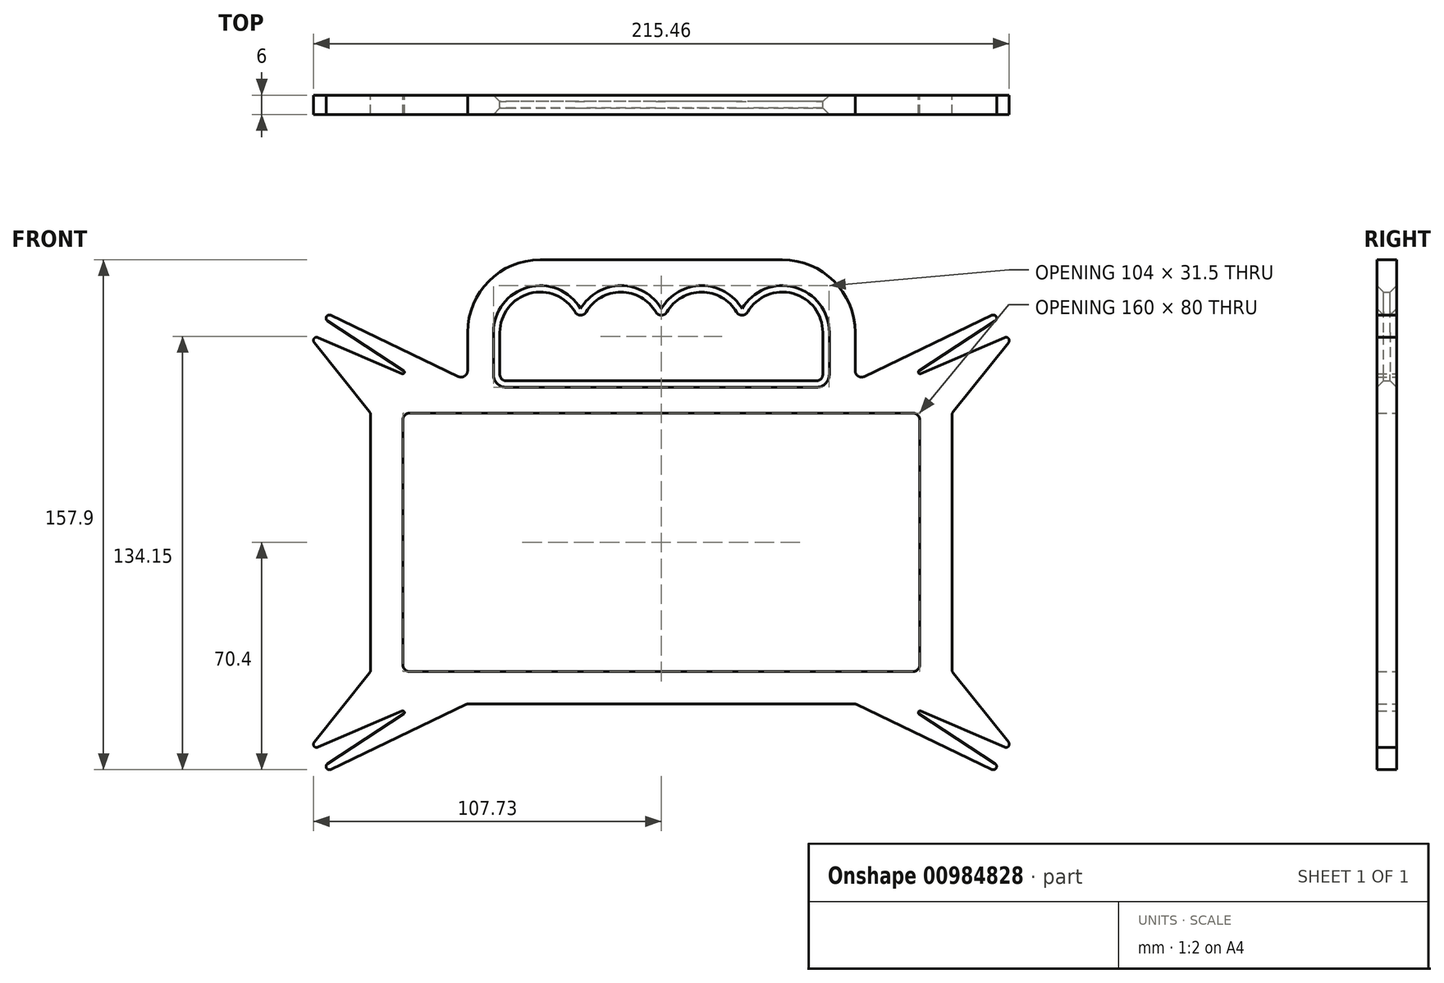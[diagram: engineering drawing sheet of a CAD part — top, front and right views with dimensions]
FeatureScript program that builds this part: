
annotation { "Feature Type Name" : "Feature", "Feature Type Description" : "" }
export const myFeature = defineFeature(function(context is Context, id is Id, definition is map)
    precondition{}
    {
        {
            var Q0;
            Q0=qCreatedBy(makeId("Front.planeOp"),FACE);
            var sketch = newSketch(context, id + "F0", { "sketchPlane" : qUnion([Q0])});
            skLineSegment(sketch, "E0.bottom", {"start": v(78, 40) * mm, "end": v(-78, 40) * mm});
            skLineSegment(sketch, "E0.top", {"start": v(78, -40) * mm, "end": v(-78, -40) * mm});
            skLineSegment(sketch, "E0.left", {"start": v(80, 38) * mm, "end": v(80, -38) * mm});
            skLineSegment(sketch, "E0.right", {"start": v(-80, 38) * mm, "end": v(-80, -38) * mm});
            skPoint(sketch, "E0.middle", {"position": v(0, 0) * mm});
            skLineSegment(sketch, "E1.top", {"start": v(60, -50) * mm, "end": v(-60, -50) * mm});
            skLineSegment(sketch, "E1.left", {"start": v(90, 39.3) * mm, "end": v(90, -40) * mm});
            skLineSegment(sketch, "E1.right", {"start": v(-90, 40) * mm, "end": v(-90, -40) * mm});
            skLineSegment(sketch, "E2", {"start": v(80.25, 52.25) * mm, "end": v(106.33, 63.43) * mm});
            skLineSegment(sketch, "E3", {"start": v(107.5, 61.88) * mm, "end": v(90.44, 40.55) * mm});
            skPoint(sketch, "E4.visualSharp", {"position": v(110, 65) * mm});
            skArc(sketch, "E4.filletArc", {"start": v(107.5, 61.88) * mm, "mid": v(107.52, 63.11) * mm, "end": v(106.33, 63.43) * mm});
            skLineSegment(sketch, "E5", {"start": v(79.78, 53.13) * mm, "end": v(103.37, 68.56) * mm});
            skLineSegment(sketch, "E6", {"start": v(102.39, 70.3) * mm, "end": v(62.86, 51.37) * mm});
            skPoint(sketch, "E7.visualSharp", {"position": v(75, 50) * mm});
            skArc(sketch, "E7.filletArc", {"start": v(79.78, 53.13) * mm, "mid": v(79.62, 52.47) * mm, "end": v(80.25, 52.25) * mm});
            skPoint(sketch, "E8.visualSharp", {"position": v(115.95, 76.8) * mm});
            skArc(sketch, "E8.filletArc", {"start": v(103.37, 68.56) * mm, "mid": v(103.7, 69.9) * mm, "end": v(102.39, 70.3) * mm});
            skPoint(sketch, "E9.newPointA", {"position": v(60, 50) * mm});
            skPoint(sketch, "E9.newPointB", {"position": v(90, 50) * mm});
            skPoint(sketch, "E10.visualSharp", {"position": v(80, 40) * mm});
            skArc(sketch, "E10.filletArc", {"start": v(80, 38) * mm, "mid": v(79.41, 39.41) * mm, "end": v(78, 40) * mm});
            skPoint(sketch, "E11.newPointA", {"position": v(90, 40) * mm});
            skArc(sketch, "E11.filletArc", {"start": v(90.44, 40.55) * mm, "mid": v(90.11, 39.96) * mm, "end": v(90, 39.3) * mm});
            skArc(sketch, "E12.MirrorCS", {"start": v(-79.78, 53.13) * mm, "mid": v(-79.62, 52.47) * mm, "end": v(-80.25, 52.25) * mm});
            skArc(sketch, "E13.MirrorCS", {"start": v(-107.5, 61.88) * mm, "mid": v(-107.52, 63.11) * mm, "end": v(-106.33, 63.43) * mm});
            skArc(sketch, "E14.MirrorCS", {"start": v(-80, 38) * mm, "mid": v(-79.41, 39.41) * mm, "end": v(-78, 40) * mm});
            skArc(sketch, "E15.MirrorCS", {"start": v(-103.37, 68.56) * mm, "mid": v(-103.7, 69.9) * mm, "end": v(-102.39, 70.3) * mm});
            skArc(sketch, "E16.MirrorCS", {"start": v(-59.55, 50) * mm, "mid": v(-59.99, 50.05) * mm, "end": v(-60.4, 50.2) * mm});
            skArc(sketch, "E17.MirrorCS", {"start": v(-90.44, 40.55) * mm, "mid": v(-90.11, 39.96) * mm, "end": v(-90, 39.3) * mm});
            skPoint(sketch, "E18.MirrorP", {"position": v(-110, 65) * mm});
            skLineSegment(sketch, "E19.MirrorCS", {"start": v(-80.25, 52.25) * mm, "end": v(-106.33, 63.43) * mm});
            skPoint(sketch, "E20.MirrorP", {"position": v(-80, 40) * mm});
            skPoint(sketch, "E21.MirrorP", {"position": v(-90, 40) * mm});
            skPoint(sketch, "E22.MirrorP", {"position": v(-75, 50) * mm});
            skPoint(sketch, "E23.MirrorP", {"position": v(-60, 50) * mm});
            skLineSegment(sketch, "E24.MirrorCS", {"start": v(-102.39, 70.3) * mm, "end": v(-62.86, 51.37) * mm});
            skLineSegment(sketch, "E25.MirrorCS", {"start": v(-107.5, 61.88) * mm, "end": v(-90.44, 40.55) * mm});
            skLineSegment(sketch, "E26.MirrorCS", {"start": v(-79.78, 53.13) * mm, "end": v(-103.37, 68.56) * mm});
            skPoint(sketch, "E27.MirrorP", {"position": v(-115.95, 76.8) * mm});
            skPoint(sketch, "E28.MirrorP", {"position": v(-90, 50) * mm});
            skLineSegment(sketch, "E29.MirrorCS", {"start": v(-90, 39.3) * mm, "end": v(-90, -40) * mm});
            skArc(sketch, "E30.MirrorCS", {"start": v(-90.44, -40.55) * mm, "mid": v(-90.11, -39.96) * mm, "end": v(-90, -39.3) * mm});
            skArc(sketch, "E31.MirrorCS", {"start": v(-59.55, -50) * mm, "mid": v(-59.99, -50.05) * mm, "end": v(-60.4, -50.2) * mm});
            skArc(sketch, "E32.MirrorCS", {"start": v(-107.5, -61.88) * mm, "mid": v(-107.52, -63.11) * mm, "end": v(-106.33, -63.43) * mm});
            skArc(sketch, "E33.MirrorCS", {"start": v(-103.37, -68.56) * mm, "mid": v(-103.7, -69.9) * mm, "end": v(-102.39, -70.3) * mm});
            skArc(sketch, "E34.MirrorCS", {"start": v(-79.78, -53.13) * mm, "mid": v(-79.62, -52.47) * mm, "end": v(-80.25, -52.25) * mm});
            skArc(sketch, "E35.MirrorCS", {"start": v(-80, -38) * mm, "mid": v(-79.41, -39.41) * mm, "end": v(-78, -40) * mm});
            skArc(sketch, "E36.MirrorCS", {"start": v(79.78, -53.13) * mm, "mid": v(79.62, -52.47) * mm, "end": v(80.25, -52.25) * mm});
            skArc(sketch, "E37.MirrorCS", {"start": v(107.5, -61.88) * mm, "mid": v(107.52, -63.11) * mm, "end": v(106.33, -63.43) * mm});
            skArc(sketch, "E38.MirrorCS", {"start": v(103.37, -68.56) * mm, "mid": v(103.7, -69.9) * mm, "end": v(102.39, -70.3) * mm});
            skArc(sketch, "E39.MirrorCS", {"start": v(59.55, -50) * mm, "mid": v(59.99, -50.05) * mm, "end": v(60.4, -50.2) * mm});
            skArc(sketch, "E40.MirrorCS", {"start": v(80, -38) * mm, "mid": v(79.41, -39.41) * mm, "end": v(78, -40) * mm});
            skArc(sketch, "E41.MirrorCS", {"start": v(90.44, -40.55) * mm, "mid": v(90.11, -39.96) * mm, "end": v(90, -39.3) * mm});
            skPoint(sketch, "E42.MirrorP", {"position": v(-90, -40) * mm});
            skPoint(sketch, "E43.MirrorP", {"position": v(-110, -65) * mm});
            skPoint(sketch, "E44.MirrorP", {"position": v(-60, -50) * mm});
            skPoint(sketch, "E45.MirrorP", {"position": v(-80, -40) * mm});
            skLineSegment(sketch, "E46.MirrorCS", {"start": v(-80.25, -52.25) * mm, "end": v(-106.33, -63.43) * mm});
            skLineSegment(sketch, "E47.MirrorCS", {"start": v(-107.5, -61.88) * mm, "end": v(-90.44, -40.55) * mm});
            skLineSegment(sketch, "E48.MirrorCS", {"start": v(-79.78, -53.13) * mm, "end": v(-103.37, -68.56) * mm});
            skPoint(sketch, "E49.MirrorP", {"position": v(-75, -50) * mm});
            skLineSegment(sketch, "E50.MirrorCS", {"start": v(-102.39, -70.3) * mm, "end": v(-60.4, -50.2) * mm});
            skPoint(sketch, "E51.MirrorP", {"position": v(-115.95, -76.8) * mm});
            skPoint(sketch, "E52.MirrorP", {"position": v(-90, -50) * mm});
            skLineSegment(sketch, "E53.MirrorCS", {"start": v(102.39, -70.3) * mm, "end": v(60.4, -50.2) * mm});
            skLineSegment(sketch, "E54.MirrorCS", {"start": v(79.78, -53.13) * mm, "end": v(103.37, -68.56) * mm});
            skPoint(sketch, "E55.MirrorP", {"position": v(115.95, -76.8) * mm});
            skLineSegment(sketch, "E56.MirrorCS", {"start": v(107.5, -61.88) * mm, "end": v(90.44, -40.55) * mm});
            skPoint(sketch, "E57.MirrorP", {"position": v(60, -50) * mm});
            skLineSegment(sketch, "E58.MirrorCS", {"start": v(80.25, -52.25) * mm, "end": v(106.33, -63.43) * mm});
            skLineSegment(sketch, "E59.MirrorCS", {"start": v(59.55, -50) * mm, "end": v(-60, -50) * mm});
            skPoint(sketch, "E60.MirrorP", {"position": v(110, -65) * mm});
            skLineSegment(sketch, "E61.MirrorCS", {"start": v(-59.55, -50) * mm, "end": v(60, -50) * mm});
            skPoint(sketch, "E62.MirrorP", {"position": v(75, -50) * mm});
            skPoint(sketch, "E63.MirrorP", {"position": v(80, -40) * mm});
            skPoint(sketch, "E64.MirrorP", {"position": v(90, -50) * mm});
            skPoint(sketch, "E65.MirrorP", {"position": v(90, -40) * mm});
            skLineSegment(sketch, "E66.MirrorCS", {"start": v(-78, -40) * mm, "end": v(78, -40) * mm});
            skLineSegment(sketch, "E67.bottom", {"start": v(40, 50) * mm, "end": v(48, 50) * mm});
            skLineSegment(sketch, "E67.right", {"start": v(50, 52) * mm, "end": v(50, 65) * mm});
            skLineSegment(sketch, "E68.left", {"start": v(50, 65) * mm, "end": v(50, 52) * mm});
            skLineSegment(sketch, "E68.right", {"start": v(60, 65) * mm, "end": v(60, 53.18) * mm});
            skArc(sketch, "E69", {"start": v(1.72, 71.33) * mm, "mid": v(12.5, 77.5) * mm, "end": v(23.28, 71.33) * mm});
            skArc(sketch, "E70", {"start": v(26.72, 71.33) * mm, "mid": v(40.78, 77.06) * mm, "end": v(50, 65) * mm});
            skLineSegment(sketch, "E71.top", {"start": v(37.5, 87.5) * mm, "end": v(0, 87.5) * mm});
            skArc(sketch, "E72", {"start": v(60, 65) * mm, "mid": v(53.4, 80.9) * mm, "end": v(37.5, 87.5) * mm});
            skPoint(sketch, "E71.left.start.orphan", {"position": v(37.5, 77.5) * mm});
            skArc(sketch, "E73.filletArc", {"start": v(48, 50) * mm, "mid": v(49.41, 50.59) * mm, "end": v(50, 52) * mm});
            skPoint(sketch, "E74.visualSharp", {"position": v(25, 65) * mm});
            skArc(sketch, "E74.filletArc", {"start": v(23.28, 71.33) * mm, "mid": v(25, 70.35) * mm, "end": v(26.72, 71.33) * mm});
            skArc(sketch, "E75.filletArc", {"start": v(60, 53.18) * mm, "mid": v(60.93, 51.48) * mm, "end": v(62.86, 51.37) * mm});
            skArc(sketch, "E76.MirrorCS", {"start": v(-48, 50) * mm, "mid": v(-49.41, 50.59) * mm, "end": v(-50, 52) * mm});
            skArc(sketch, "E77.MirrorCS", {"start": v(-60, 53.18) * mm, "mid": v(-60.93, 51.48) * mm, "end": v(-62.86, 51.37) * mm});
            skLineSegment(sketch, "E78.MirrorCS", {"start": v(-50, 52) * mm, "end": v(-50, 65) * mm});
            skPoint(sketch, "E79.MirrorP", {"position": v(-60.4, 50.2) * mm});
            skArc(sketch, "E80.MirrorCS", {"start": v(-23.28, 71.33) * mm, "mid": v(-25, 70.35) * mm, "end": v(-26.72, 71.33) * mm});
            skArc(sketch, "E81.MirrorCS", {"start": v(-60, 65) * mm, "mid": v(-53.4, 80.9) * mm, "end": v(-37.5, 87.5) * mm});
            skArc(sketch, "E82.MirrorCS", {"start": v(-26.72, 71.33) * mm, "mid": v(-40.78, 77.06) * mm, "end": v(-50, 65) * mm});
            skLineSegment(sketch, "E83.MirrorCS", {"start": v(-25, 50) * mm, "end": v(0, 50) * mm});
            skLineSegment(sketch, "E84.MirrorCS", {"start": v(-60, 65) * mm, "end": v(-60, 53.18) * mm});
            skLineSegment(sketch, "E85.MirrorCS", {"start": v(-50, 65) * mm, "end": v(-50, 52) * mm});
            skLineSegment(sketch, "E86.MirrorCS", {"start": v(-59.55, 50) * mm, "end": v(-60, 50) * mm});
            skPoint(sketch, "E87.MirrorP", {"position": v(-37.5, 77.5) * mm});
            skLineSegment(sketch, "E88.MirrorCS", {"start": v(-37.5, 87.5) * mm, "end": v(0, 87.5) * mm});
            skLineSegment(sketch, "E89.MirrorCS", {"start": v(-40, 50) * mm, "end": v(-48, 50) * mm});
            skArc(sketch, "E90.MirrorCS", {"start": v(-1.72, 71.33) * mm, "mid": v(-12.5, 77.5) * mm, "end": v(-23.28, 71.33) * mm});
            skPoint(sketch, "E91.MirrorP", {"position": v(-25, 65) * mm});
            skPoint(sketch, "E92.MirrorCS.start.orphan", {"position": v(0, 77.5) * mm});
            skPoint(sketch, "E93.visualSharp", {"position": v(0, 65) * mm});
            skArc(sketch, "E93.filletArc", {"start": v(-1.72, 71.33) * mm, "mid": v(0, 70.35) * mm, "end": v(1.72, 71.33) * mm});
            skPoint(sketch, "E94.orphan", {"position": v(-50, 50) * mm});
            skLineSegment(sketch, "E95.trimOffspring", {"start": v(-40, 50) * mm, "end": v(-25, 50) * mm});
            skPoint(sketch, "E96.orphan", {"position": v(50, 50) * mm});
            skPoint(sketch, "E68.top.start.orphan", {"position": v(59.55, 50) * mm});
            skLineSegment(sketch, "E97.trimOffspring", {"start": v(0, 50) * mm, "end": v(40, 50) * mm});
            skPoint(sketch, "E98.top.end.orphan", {"position": v(0, 50) * mm});
            skPoint(sketch, "E98.top.start.orphan", {"position": v(25, 50) * mm});
            skSolve(sketch);
        }
        {
            var Q0;
            Q0=makeQuery(id+"F0.imprint","IMPRINT",FACE,{"disambiguationData":[TD([[makeQuery(id+"F0.imprint","IMPRINT",EDGE,{"derivedFrom":sQuery(id+"F0.wireOp",EDGE,"E0.bottom")}),-1.0]])]});
            extrude(context, id + "F1", {"entities" : qUnion([Q0]), "depth" : 6 * mm, "offsetDistance" : 25 * mm});
        }
        {
            var Q0;
            Q0=makeQuery(id+"F1.opExtrude","CAP_EDGE",EDGE,{"disambiguationData":[OSD([sQuery(id+"F0.wireOp",EDGE,"E67.bottom"),sQuery(id+"F0.wireOp",EDGE,"E83.MirrorCS"),sQuery(id+"F0.wireOp",EDGE,"E89.MirrorCS"),sQuery(id+"F0.wireOp",EDGE,"E95.trimOffspring"),sQuery(id+"F0.wireOp",EDGE,"E97.trimOffspring")])],"isStart":false});
            var Q1;
            Q1=makeQuery(id+"F1.opExtrude","CAP_EDGE",EDGE,{"disambiguationData":[OSD([sQuery(id+"F0.wireOp",EDGE,"E67.bottom"),sQuery(id+"F0.wireOp",EDGE,"E83.MirrorCS"),sQuery(id+"F0.wireOp",EDGE,"E89.MirrorCS"),sQuery(id+"F0.wireOp",EDGE,"E95.trimOffspring"),sQuery(id+"F0.wireOp",EDGE,"E97.trimOffspring")])],"isStart":true});
            chamfer(context, id + "F2", {"entities" : qUnion([Q0, Q1]), "width" : 2 * mm, "tangentPropagation" : true});
        }
    });
